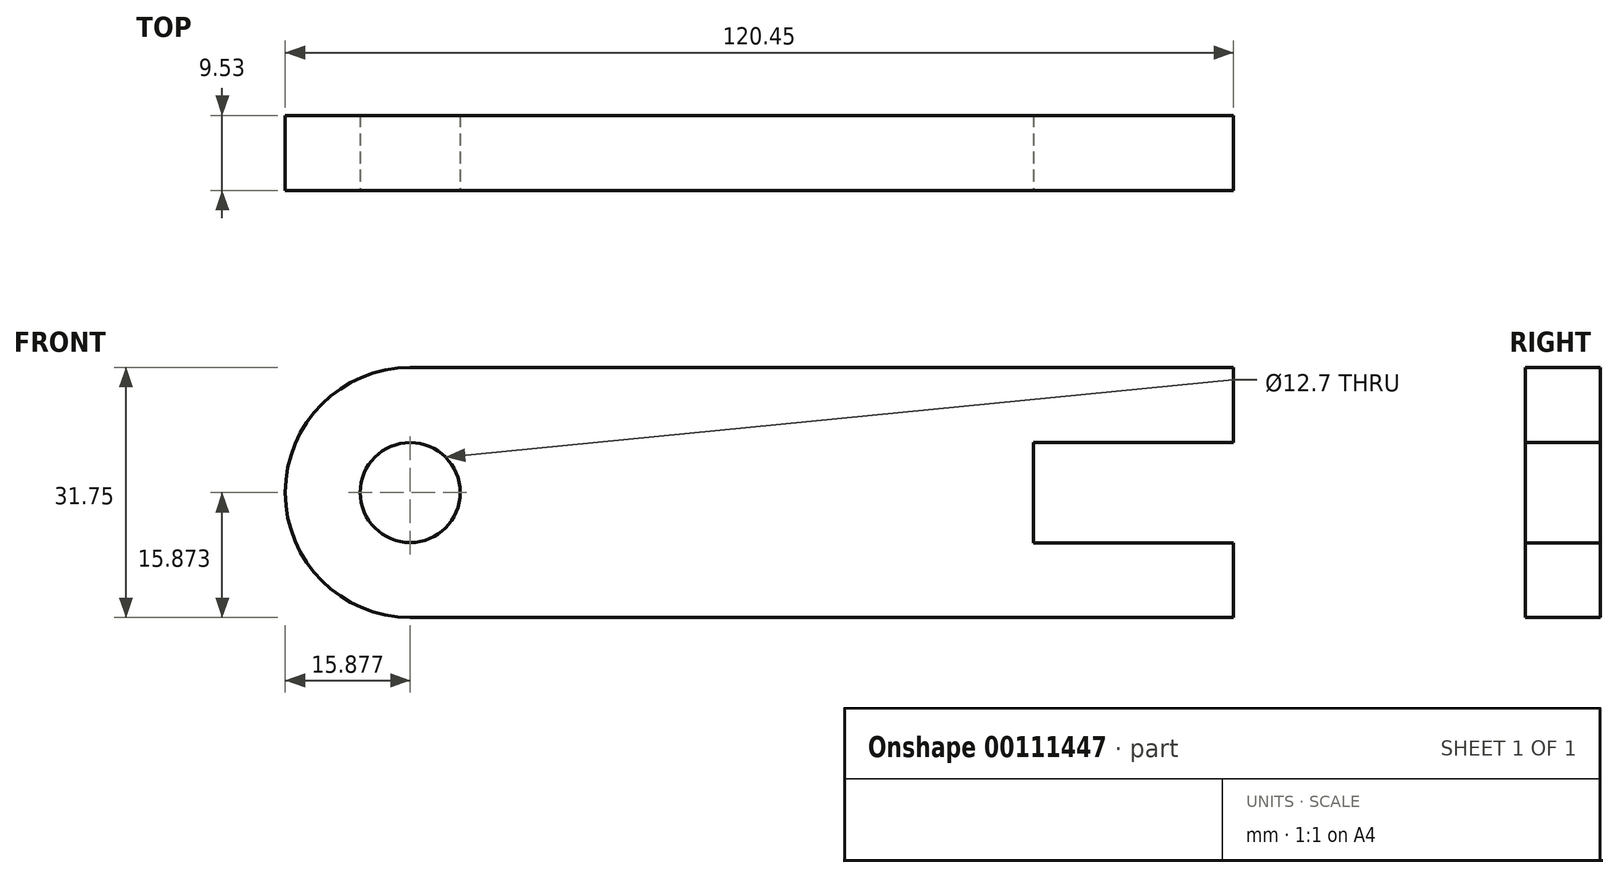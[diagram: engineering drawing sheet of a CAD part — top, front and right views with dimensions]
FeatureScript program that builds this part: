
annotation { "Feature Type Name" : "Feature", "Feature Type Description" : "" }
export const myFeature = defineFeature(function(context is Context, id is Id, definition is map)
    precondition{}
    {
        {
            var Q0;
            Q0=qCreatedBy(makeId("Front.planeOp"),FACE);
            var sketch = newSketch(context, id + "F0", { "sketchPlane" : qUnion([Q0])});
            skLineSegment(sketch, "E0", {"start": v(-61.05, -15.11) * mm, "end": v(43.52, -15.11) * mm});
            skLineSegment(sketch, "E1", {"start": v(43.52, -15.11) * mm, "end": v(43.52, -5.63) * mm});
            skLineSegment(sketch, "E2", {"start": v(43.52, -5.63) * mm, "end": v(18.12, -5.63) * mm});
            skLineSegment(sketch, "E3", {"start": v(18.12, -5.63) * mm, "end": v(18.12, 7.15) * mm});
            skLineSegment(sketch, "E4", {"start": v(18.12, 7.15) * mm, "end": v(43.52, 7.15) * mm});
            skLineSegment(sketch, "E5", {"start": v(43.52, 7.15) * mm, "end": v(43.52, 16.64) * mm});
            skLineSegment(sketch, "E6", {"start": v(43.52, 16.64) * mm, "end": v(18.12, 16.64) * mm});
            skLineSegment(sketch, "E7", {"start": v(18.12, 16.64) * mm, "end": v(-61.05, 16.64) * mm});
            skArc(sketch, "E8", {"start": v(-61.05, 16.64) * mm, "mid": v(-76.93, 0.76) * mm, "end": v(-61.05, -15.11) * mm});
            skCircle(sketch, "E9", {"center": v(-61.05, 0.76) * mm, "radius": 6.35 * mm});
            skSolve(sketch);
        }
        {
            var Q0;
            Q0=makeQuery(id+"F0.imprint","IMPRINT",FACE,{"disambiguationData":[TD([[makeQuery(id+"F0.imprint","IMPRINT",EDGE,{"derivedFrom":sQuery(id+"F0.wireOp",EDGE,"E0")}),1.0]])]});
            extrude(context, id + "F1", {"entities" : qUnion([Q0]), "oppositeDirection" : true, "depth" : 9.52 * mm});
        }
    });
